# Revit family: E_Cable Tray Support_MEPcontent_OBO Bettermann_US3 FT
name_source: partatom
category: Cable Tray Fittings
revit_build: Autodesk Revit MEP 2015 (Build: 20140606_1530(x64)
units: mm (PartAtom-declared; Revit-internal decimal feet)

## types (11) — shared parameters
Article Description = Suspended support (U profile) of dimensions 50 x 30 mm with welded head plate.
Depth = 40 mm  [stored 0.131234 ft]
Description = Suspended support (U profile) of dimensions 50 x 30 mm with welded head plate.
EMCS Version = 2.0
ETIM Article Class = EC000082
Family Version = 10.14
Gray = Color RGB 189-187-185
IFCExportAs = IfcCableCarrierFittingType
IFCExportType = NOTDEFINED
MEPcontent Class = CABLE_TRAY_SUPPORT
Manufacturer = OBO BETTERMANN
Manufacturer URL = http://catalog4.obo-bettermann.com
Product Line = OBO BETTERMANN CableTrays
Revit Version = 2015
URL = www.stabiplan.com
Width 1 = 50 mm  [stored 0.164042 ft]
Width 2 = 30 mm  [stored 0.0984252 ft]

## per-type parameters (varying)
| type | GTIN | Height 1 | Manufacturer Art. No. |
| US 3 K 20 FT | 4012196224470 | 200 mm  [stored 0.656168 ft] | 6342351 |
| US 3 K 30 FT | 4012196224531 | 300 mm | 6342353 |
| US 3 K 40 FT | 4012196224593 | 400 mm  [stored 1.31234 ft] | 6342355 |
| US 3 K 50 FT | 4012196224654 | 500 mm  [stored 1.64042 ft] | 6342357 |
| US 3 K 60 FT | 4012196224715 | 600 mm | 6342359 |
| US 3 K 70 FT | 4012196224777 | 700 mm  [stored 2.29659 ft] | 6342362 |
| US 3 K 80 FT | 4012196225019 | 800 mm  [stored 2.62467 ft] | 6342364 |
| US 3 K 90 FT | 4012196225071 | 900 mm  [stored 2.95276 ft] | 6342366 |
| US 3 K 100 FT | 4012196225132 | 1000 mm  [stored 3.28084 ft] | 6342368 |
| US 3 K 110 FT | 4012196225378 | 1100 mm  [stored 3.60892 ft] | 6342370 |
| US 3 K 120 FT | 4012196225439 | 1200 mm | 6342372 |

note: column(s) folded — value = type name in every type: Article Type, Model

note: [stored X ft] marks values corroborated as IEEE doubles in the binary element streams (Revit-internal decimal feet)

## geometry (parser evidence)
native form markers: Blend x4, Sweep x3
no freeform markers — native parametric forms only
